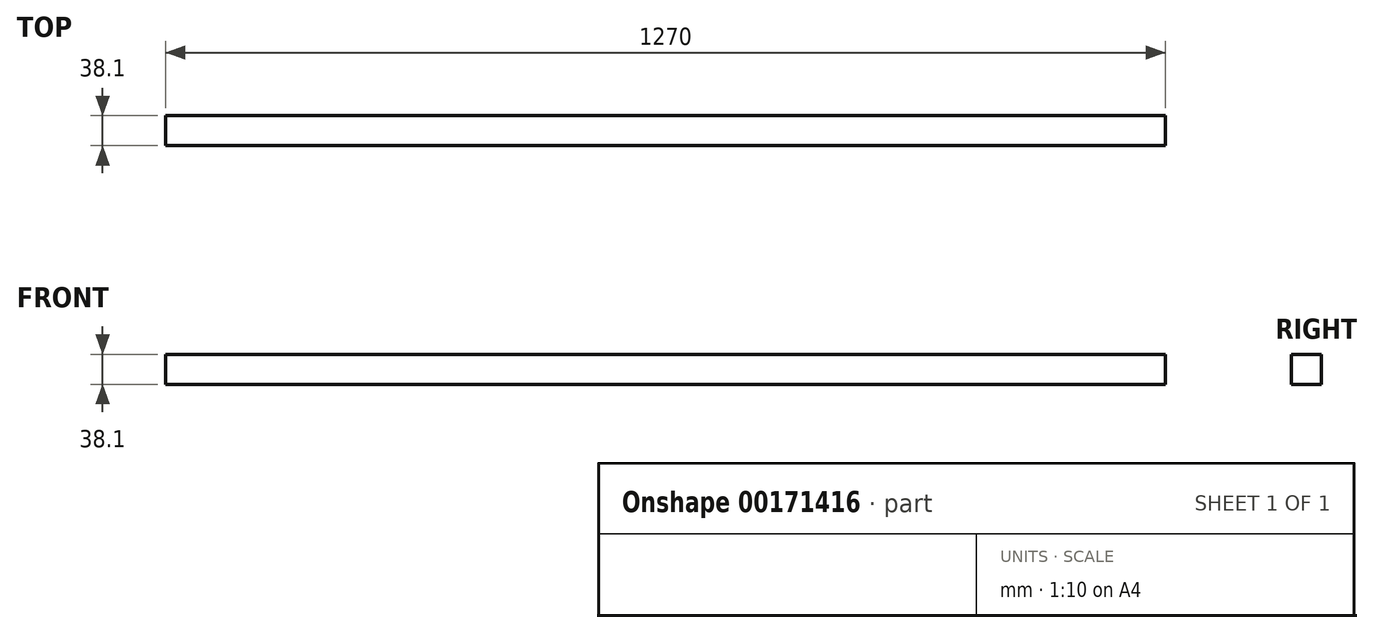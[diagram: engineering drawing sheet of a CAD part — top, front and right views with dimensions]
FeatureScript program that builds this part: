
annotation { "Feature Type Name" : "Feature", "Feature Type Description" : "" }
export const myFeature = defineFeature(function(context is Context, id is Id, definition is map)
    precondition{}
    {
        {
            var Q0;
            Q0=qCreatedBy(makeId("Top.planeOp"),FACE);
            var sketch = newSketch(context, id + "F0", { "sketchPlane" : qUnion([Q0])});
            skLineSegment(sketch, "E0.bottom", {"start": v(-635, 19.05) * mm, "end": v(635, 19.05) * mm});
            skLineSegment(sketch, "E0.top", {"start": v(-635, -19.05) * mm, "end": v(635, -19.05) * mm});
            skLineSegment(sketch, "E0.left", {"start": v(-635, 19.05) * mm, "end": v(-635, -19.05) * mm});
            skLineSegment(sketch, "E0.right", {"start": v(635, 19.05) * mm, "end": v(635, -19.05) * mm});
            skPoint(sketch, "E0.middle", {"position": v(0, 0) * mm});
            skSolve(sketch);
        }
        {
            var Q0;
            Q0 = qSketchRegion(id + "F0", true);
            extrude(context, id + "F1", {"entities" : qUnion([Q0]), "depth" : 38.1 * mm});
        }
    });
